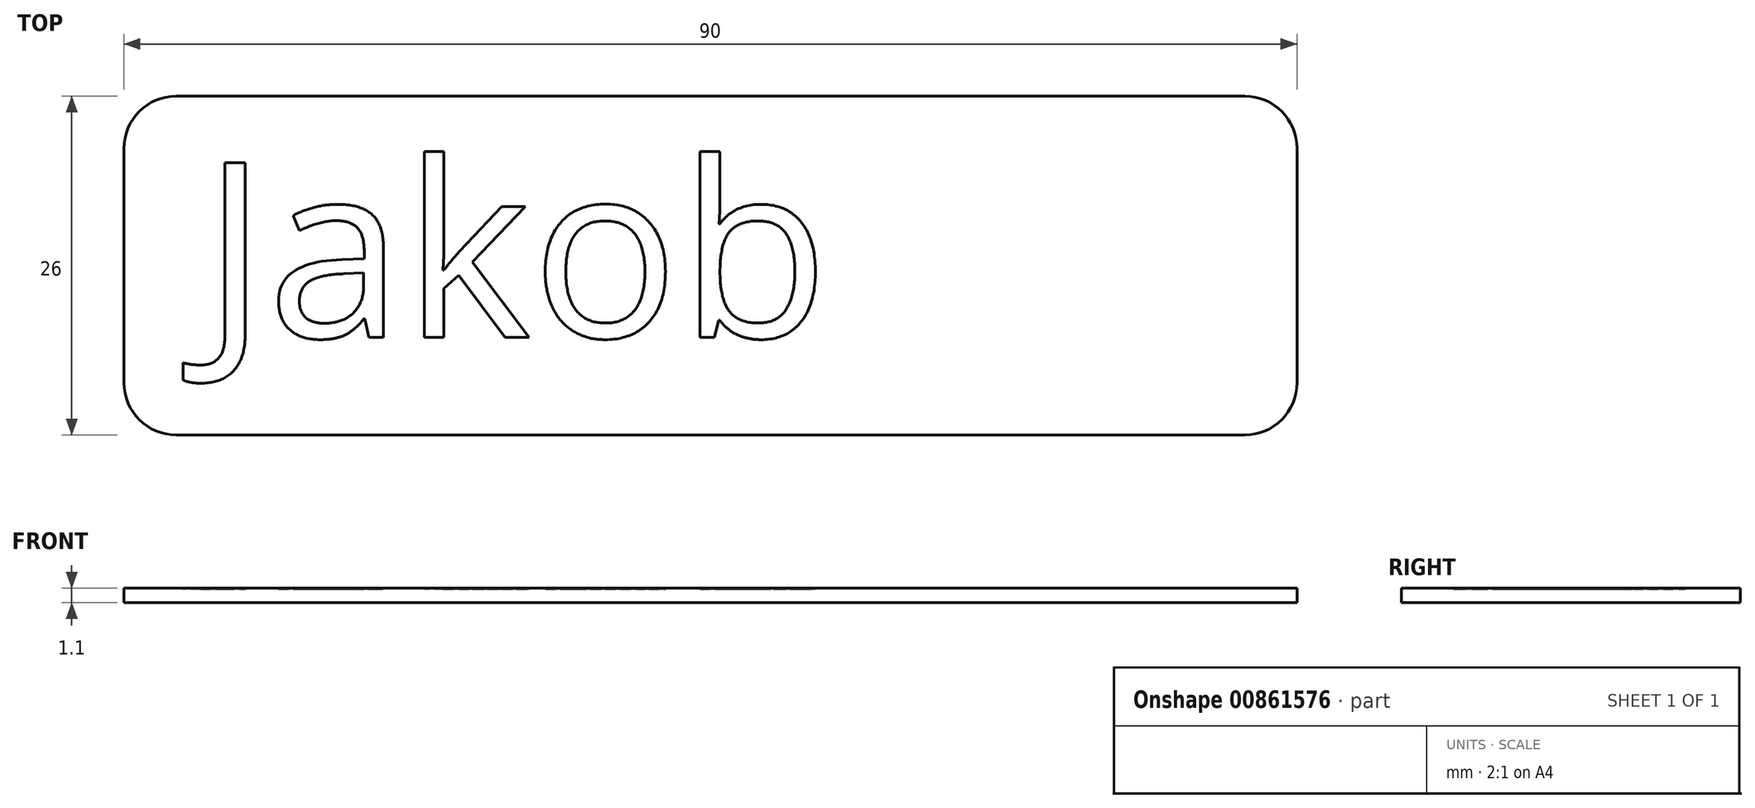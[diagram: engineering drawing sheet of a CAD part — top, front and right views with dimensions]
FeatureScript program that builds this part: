
annotation { "Feature Type Name" : "Feature", "Feature Type Description" : "" }
export const myFeature = defineFeature(function(context is Context, id is Id, definition is map)
    precondition{}
    {
        {
            var Q0;
            Q0=qCreatedBy(makeId("Top.planeOp"),FACE);
            var sketch = newSketch(context, id + "F0", { "sketchPlane" : qUnion([Q0])});
            skLineSegment(sketch, "E0.bottom", {"start": v(41, 13) * mm, "end": v(-41, 13) * mm});
            skLineSegment(sketch, "E0.top", {"start": v(41, -13) * mm, "end": v(-41, -13) * mm});
            skLineSegment(sketch, "E0.left", {"start": v(45, 9) * mm, "end": v(45, -9) * mm});
            skLineSegment(sketch, "E0.right", {"start": v(-45, 9) * mm, "end": v(-45, -9) * mm});
            skPoint(sketch, "E0.middle", {"position": v(0, 0) * mm});
            skPoint(sketch, "E1.visualSharp", {"position": v(-45, 13) * mm});
            skArc(sketch, "E1.filletArc", {"start": v(-41, 13) * mm, "mid": v(-43.83, 11.83) * mm, "end": v(-45, 9) * mm});
            skPoint(sketch, "E2.visualSharp", {"position": v(45, 13) * mm});
            skArc(sketch, "E2.filletArc", {"start": v(45, 9) * mm, "mid": v(43.83, 11.83) * mm, "end": v(41, 13) * mm});
            skPoint(sketch, "E3.visualSharp", {"position": v(45, -13) * mm});
            skArc(sketch, "E3.filletArc", {"start": v(41, -13) * mm, "mid": v(43.83, -11.83) * mm, "end": v(45, -9) * mm});
            skPoint(sketch, "E4.visualSharp", {"position": v(-45, -13) * mm});
            skArc(sketch, "E4.filletArc", {"start": v(-45, -9) * mm, "mid": v(-43.83, -11.83) * mm, "end": v(-41, -13) * mm});
            skSolve(sketch);
        }
        {
            var Q0;
            Q0=makeQuery(id+"F0.imprint","IMPRINT",FACE,{"disambiguationData":[TD([[makeQuery(id+"F0.imprint","IMPRINT",EDGE,{"derivedFrom":sQuery(id+"F0.wireOp",EDGE,"E0.bottom")}),1.0]])]});
            extrude(context, id + "F1", {"entities" : qUnion([Q0]), "depth" : 1 * mm, "offsetDistance" : 25 * mm});
        }
        {
            var Q0;
            Q0=makeQuery(id+"F1.opExtrude","CAP_FACE",FACE,{"disambiguationData":[OSD([sQuery(id+"F0.wireOp",EDGE,"E0.bottom"),sQuery(id+"F0.wireOp",EDGE,"E0.top"),sQuery(id+"F0.wireOp",EDGE,"E0.left"),sQuery(id+"F0.wireOp",EDGE,"E0.right")])],"isStart":false});
            var sketch = newSketch(context, id + "F2", { "sketchPlane" : qUnion([Q0])});
            skLineSegment(sketch, "E5.bottom", {"start": v(40, 10) * mm, "end": v(-40, 10) * mm});
            skLineSegment(sketch, "E5.top", {"start": v(40, -10) * mm, "end": v(-40, -10) * mm});
            skLineSegment(sketch, "E5.left", {"start": v(42, 8) * mm, "end": v(42, -8) * mm});
            skLineSegment(sketch, "E5.right", {"start": v(-42, 8) * mm, "end": v(-42, -8) * mm});
            skPoint(sketch, "E5.middle", {"position": v(0, 0) * mm});
            skPoint(sketch, "E6.visualSharp", {"position": v(-42, 10) * mm});
            skArc(sketch, "E6.filletArc", {"start": v(-40, 10) * mm, "mid": v(-41.41, 9.41) * mm, "end": v(-42, 8) * mm});
            skPoint(sketch, "E7.visualSharp", {"position": v(-42, -10) * mm});
            skArc(sketch, "E7.filletArc", {"start": v(-42, -8) * mm, "mid": v(-41.41, -9.41) * mm, "end": v(-40, -10) * mm});
            skPoint(sketch, "E8.visualSharp", {"position": v(42, -10) * mm});
            skArc(sketch, "E8.filletArc", {"start": v(40, -10) * mm, "mid": v(41.41, -9.41) * mm, "end": v(42, -8) * mm});
            skPoint(sketch, "E9.visualSharp", {"position": v(42, 10) * mm});
            skArc(sketch, "E9.filletArc", {"start": v(42, 8) * mm, "mid": v(41.41, 9.41) * mm, "end": v(40, 10) * mm});
            skText(sketch, "E10", { "text": "Jakob", "fontName": "OpenSans-Regular.ttf"});
            const initialGuessF2  = {"E10": [-0.039, -0.0055, 1, 0, 0.0135]};
            skSetInitialGuess(sketch, initialGuessF2);
            skSolve(sketch);
        }
        {
            var Q0;
            Q0=makeQuery(id+"F2.imprint","IMPRINT",FACE,{"disambiguationData":[TD([[makeQuery(id+"F2.imprint","IMPRINT",EDGE,{"derivedFrom":sQuery(id+"F2.wireOp",EDGE,"E5.bottom")}),-1.0]])]});
            var Q1;
            Q1=makeQuery(id+"F2.imprint","IMPRINT",FACE,{"disambiguationData":[TD([[makeQuery(id+"F2.imprint","IMPRINT",EDGE,{"derivedFrom":sQuery(id+"F2.wireOp",EDGE,"E5.bottom")}),1.0]])]});
            var Q2;
            Q2=makeQuery(id+"F2.imprint","IMPRINT",FACE,{"disambiguationData":[TD([[makeQuery(id+"F2.imprint","IMPRINT",EDGE,{"derivedFrom":sQuery(id+"F2.wireOp",EDGE,"E10.sketch_text.stroke-29")}),1.0]])]});
            var Q3;
            Q3=makeQuery(id+"F2.imprint","IMPRINT",FACE,{"disambiguationData":[TD([[makeQuery(id+"F2.imprint","IMPRINT",EDGE,{"derivedFrom":sQuery(id+"F2.wireOp",EDGE,"E10.sketch_text.stroke-61")}),1.0]])]});
            var Q4;
            Q4=makeQuery(id+"F2.imprint","IMPRINT",FACE,{"disambiguationData":[TD([[makeQuery(id+"F2.imprint","IMPRINT",EDGE,{"derivedFrom":sQuery(id+"F2.wireOp",EDGE,"E10.sketch_text.stroke-84")}),1.0]])]});
            extrude(context, id + "F3", {"entities" : qUnion([Q0, Q1, Q2, Q3, Q4]), "operationType" : NewBodyOperationType.ADD, "depth" : .1 * mm, "offsetDistance" : 25 * mm});
        }
    });
